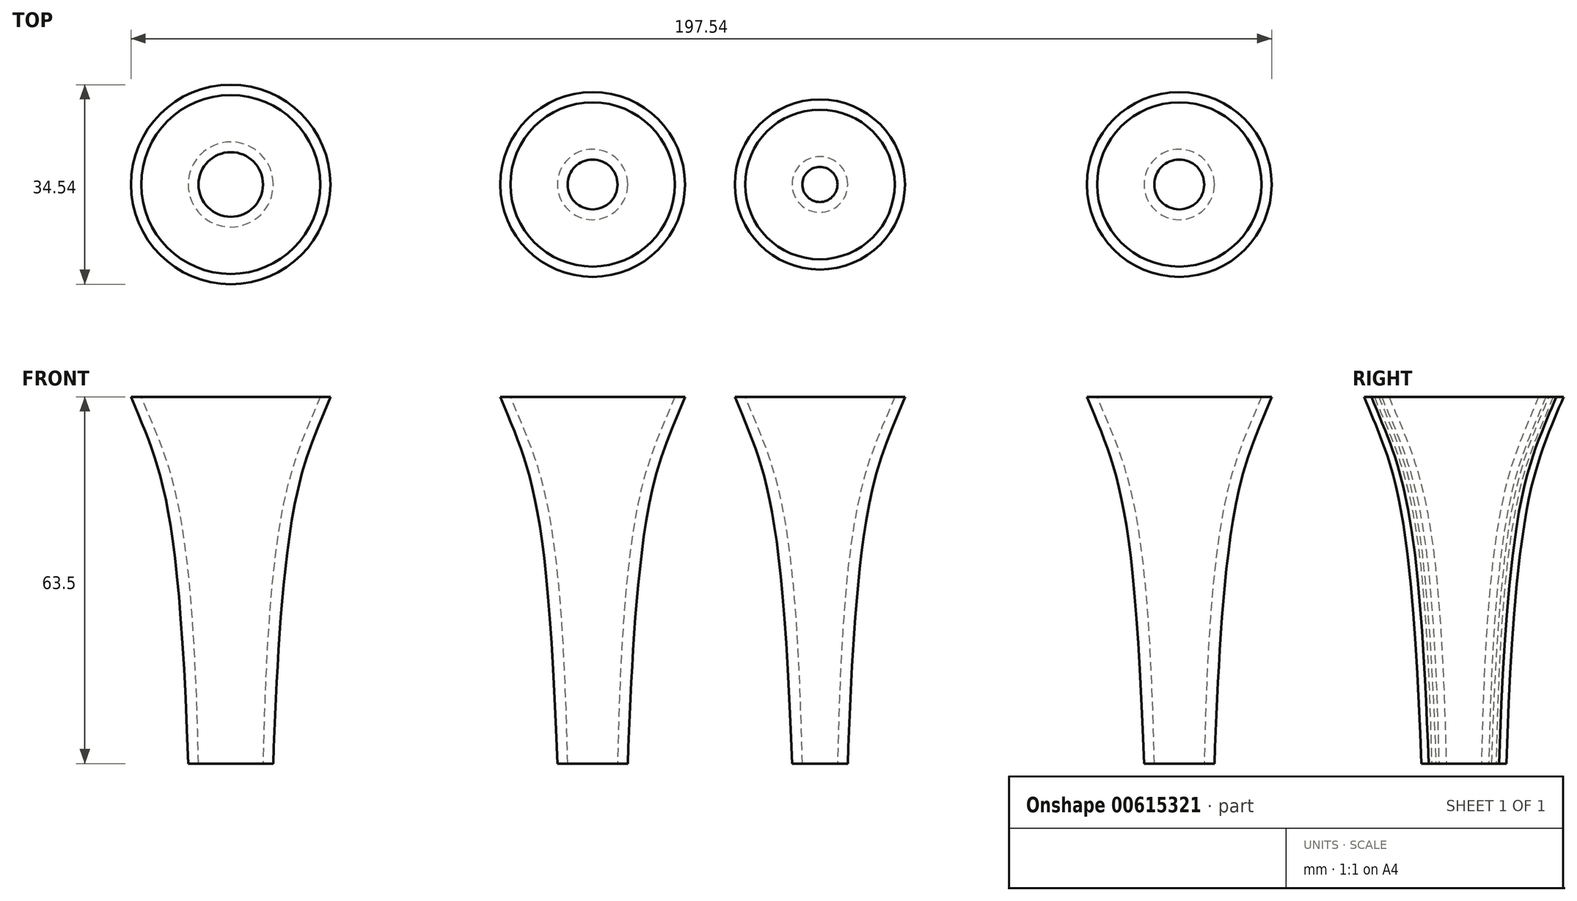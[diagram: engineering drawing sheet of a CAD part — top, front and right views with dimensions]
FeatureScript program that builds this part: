
annotation { "Feature Type Name" : "Feature", "Feature Type Description" : "" }
export const myFeature = defineFeature(function(context is Context, id is Id, definition is map)
    precondition{}
    {
        {
            var Q0;
            Q0=qCreatedBy(makeId("Front.planeOp"),FACE);
            var sketch = newSketch(context, id + "F0", { "sketchPlane" : qUnion([Q0])});
            skFitSpline(sketch, "E0", {"points": [v(4.32, 0) * mm, v(14.22, 63.5) * mm], "startDerivative": vector(3, 139.3) * mm, "endDerivative": vector(15.08, 37.1) * mm});
            skFitSpline(sketch, "E1", {"points": [v(6.1, 0) * mm, v(16, 63.5) * mm], "startDerivative": vector(4.89, 140.6) * mm, "endDerivative": vector(15.08, 37.1) * mm});
            skLineSegment(sketch, "E2", {"start": v(14.22, 63.5) * mm, "end": v(16, 63.5) * mm});
            skLineSegment(sketch, "E3", {"start": v(4.32, 0) * mm, "end": v(6.1, 0) * mm});
            skLineSegment(sketch, "E4", {"start": v(0, 27.84) * mm, "end": v(0, 73.77) * mm, "construction": true});
            skLineSegment(sketch, "E5", {"start": v(0, -31.8) * mm, "end": v(82.24, -31.8) * mm});
            skSolve(sketch);
        }
        {
            var Q0;
            Q0=makeQuery(id+"F0.imprint","IMPRINT",FACE,{"disambiguationData":[TD([[makeQuery(id+"F0.imprint","IMPRINT",EDGE,{"derivedFrom":sQuery(id+"F0.wireOp",EDGE,"E0")}),-1.0]])]});
            var Q1;
            Q1=sQuery(id+"F0.wireOp",EDGE,"E4");
            revolve(context, id + "F1", {"entities" : qUnion([Q0]), "axis" : qUnion([Q1]), "revolveType" : RevolveType.FULL});
        }
        {
            var Q0;
            Q0=qCreatedBy(makeId("Front.planeOp"),FACE);
            var sketch = newSketch(context, id + "F2", { "sketchPlane" : qUnion([Q0])});
            skFitSpline(sketch, "E6", {"points": [v(-57.08, 0) * mm, v(-47.17, 63.5) * mm], "startDerivative": vector(3, 139.3) * mm, "endDerivative": vector(15.08, 37.1) * mm});
            skFitSpline(sketch, "E7", {"points": [v(-55.3, 0) * mm, v(-45.4, 63.5) * mm], "startDerivative": vector(4.89, 140.6) * mm, "endDerivative": vector(15.08, 37.1) * mm});
            skLineSegment(sketch, "E8", {"start": v(-47.17, 63.5) * mm, "end": v(-45.4, 63.5) * mm});
            skLineSegment(sketch, "E9", {"start": v(-57.08, 0) * mm, "end": v(-55.3, 0) * mm});
            skLineSegment(sketch, "E10", {"start": v(-62.67, -41.54) * mm, "end": v(-62.67, 73.77) * mm, "construction": true});
            skSolve(sketch);
        }
        {
            var Q0;
            Q0=makeQuery(id+"F2.imprint","IMPRINT",FACE,{"disambiguationData":[TD([[makeQuery(id+"F2.imprint","IMPRINT",EDGE,{"derivedFrom":sQuery(id+"F2.wireOp",EDGE,"E6")}),-1.0]])]});
            var Q1;
            Q1=sQuery(id+"F2.wireOp",EDGE,"E10");
            revolve(context, id + "F3", {"entities" : qUnion([Q0]), "axis" : qUnion([Q1]), "revolveType" : RevolveType.FULL});
        }
        {
            var Q0;
            Q0=qCreatedBy(makeId("Front.planeOp"),FACE);
            var sketch = newSketch(context, id + "F4", { "sketchPlane" : qUnion([Q0])});
            skFitSpline(sketch, "E11", {"points": [v(42.4, 0) * mm, v(52.31, 63.5) * mm], "startDerivative": vector(3, 139.3) * mm, "endDerivative": vector(15.08, 37.1) * mm});
            skFitSpline(sketch, "E12", {"points": [v(44.18, 0) * mm, v(54.1, 63.5) * mm], "startDerivative": vector(4.89, 140.6) * mm, "endDerivative": vector(15.08, 37.1) * mm});
            skLineSegment(sketch, "E13", {"start": v(52.31, 63.5) * mm, "end": v(54.1, 63.5) * mm});
            skLineSegment(sketch, "E14", {"start": v(42.4, 0) * mm, "end": v(44.18, 0) * mm});
            skLineSegment(sketch, "E15", {"start": v(39.36, -41.54) * mm, "end": v(39.36, 73.77) * mm, "construction": true});
            skSolve(sketch);
        }
        {
            var Q0;
            Q0 = qSketchRegion(id + "F4", true);
            var Q1;
            Q1=makeQuery(id+"F4.imprint","IMPRINT",FACE,{"disambiguationData":[TD([[makeQuery(id+"F4.imprint","IMPRINT",EDGE,{"derivedFrom":sQuery(id+"F4.wireOp",EDGE,"E11")}),-1.0]])]});
            var Q2;
            Q2=sQuery(id+"F4.wireOp",EDGE,"E15");
            revolve(context, id + "F5", {"entities" : qUnion([Q0, Q1]), "axis" : qUnion([Q2]), "revolveType" : RevolveType.FULL});
        }
        {
            var Q0;
            Q0=makeQuery(id+"F1.opRevolve","SWEPT_BODY",BODY,{"disambiguationData":[OSD([sQuery(id+"F0.wireOp",EDGE,"E0"),sQuery(id+"F0.wireOp",EDGE,"E1"),sQuery(id+"F0.wireOp",EDGE,"E2"),sQuery(id+"F0.wireOp",EDGE,"E3")])]});
            transform(context, id + "F6", {"entities" : qUnion([Q0]), "transformType" : TransformType.TRANSLATION_3D, "dx" : 101.6 * mm, "dy" : 0 * mm, "dz" : 0 * mm, "makeCopy" : true});
        }
    });
